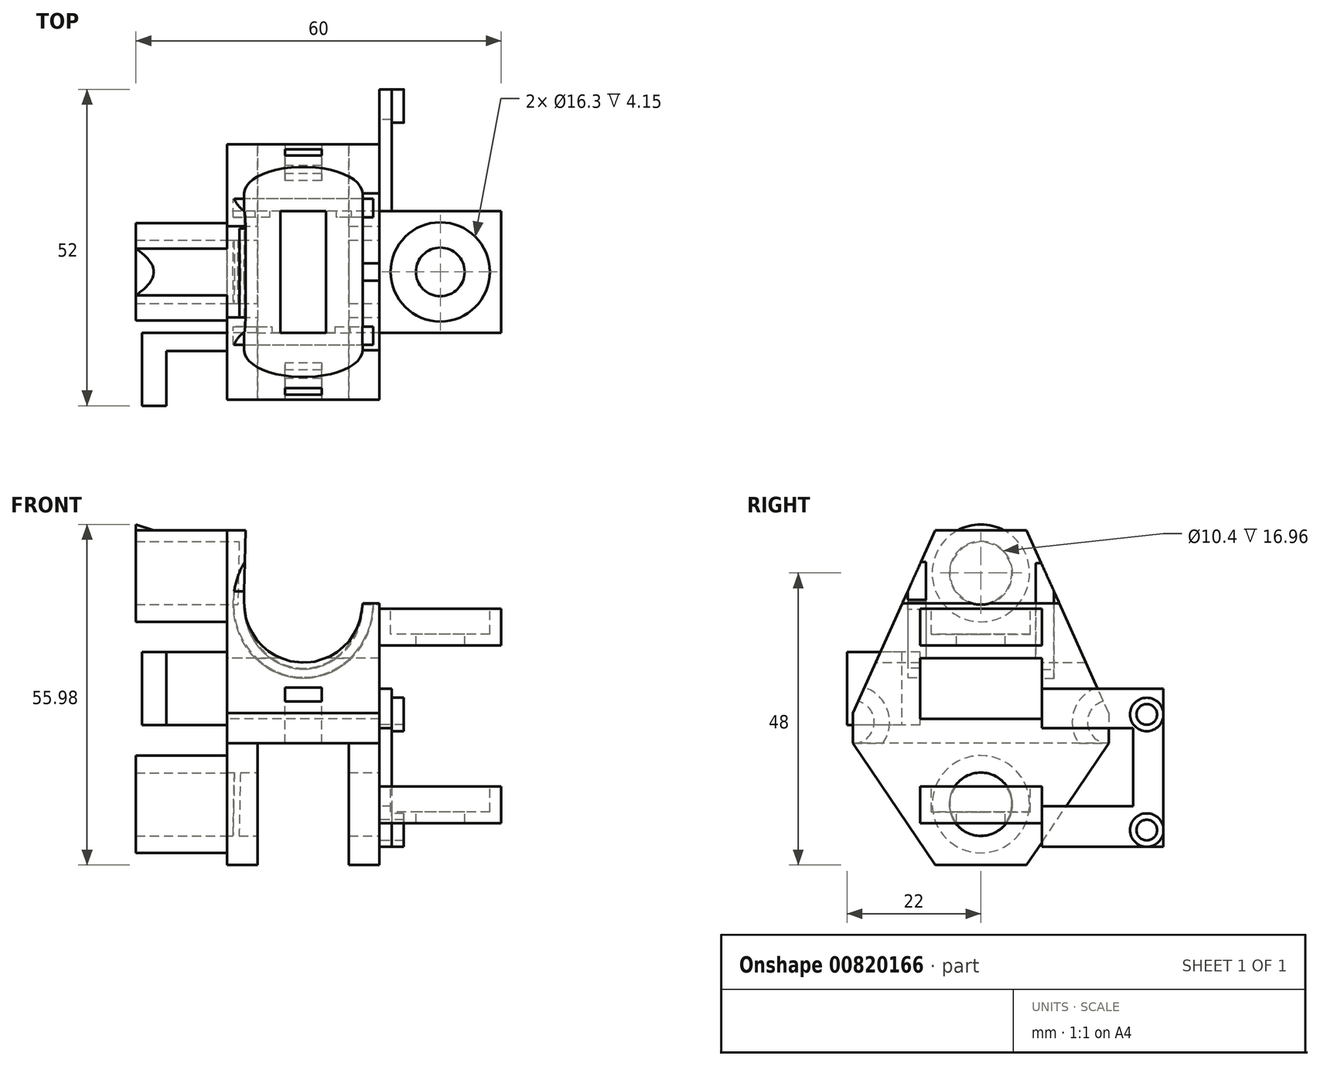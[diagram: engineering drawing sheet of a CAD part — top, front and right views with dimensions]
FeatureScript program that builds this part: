
annotation { "Feature Type Name" : "Feature", "Feature Type Description" : "" }
export const myFeature = defineFeature(function(context is Context, id is Id, definition is map)
    precondition{}
    {
        {
            var Q0;
            Q0=qCreatedBy(makeId("Top.planeOp"),FACE);
            var sketch = newSketch(context, id + "F0", { "sketchPlane" : qUnion([Q0])});
            skLineSegment(sketch, "E0.bottom", {"start": v(0, 0) * mm, "end": v(42, 0) * mm});
            skLineSegment(sketch, "E0.top", {"start": v(0, 42) * mm, "end": v(42, 42) * mm});
            skLineSegment(sketch, "E0.left", {"start": v(0, 0) * mm, "end": v(0, 42) * mm});
            skLineSegment(sketch, "E0.right", {"start": v(42, 0) * mm, "end": v(42, 12) * mm});
            skArc(sketch, "E1", {"start": v(27.05, 31.36) * mm, "mid": v(9, 21) * mm, "end": v(27.05, 10.64) * mm});
            skPoint(sketch, "E1.centerSnap0", {"position": v(21, 42) * mm});
            skPoint(sketch, "E1.centerSnap1", {"position": v(42, 21) * mm});
            skCircle(sketch, "E2", {"center": v(5.5, 36.5) * mm, "radius": 1.55 * mm});
            skCircle(sketch, "E3", {"center": v(36.5, 36.5) * mm, "radius": 1.55 * mm});
            skCircle(sketch, "E4", {"center": v(36.5, 5.5) * mm, "radius": 1.55 * mm});
            skCircle(sketch, "E5", {"center": v(5.5, 5.5) * mm, "radius": 1.55 * mm});
            skLineSegment(sketch, "E6", {"start": v(42, 30) * mm, "end": v(32.1, 30) * mm});
            skLineSegment(sketch, "E7", {"start": v(42, 12) * mm, "end": v(32.1, 12) * mm});
            skLineSegment(sketch, "E8.trimOffspring", {"start": v(42, 30) * mm, "end": v(42, 42) * mm});
            skPoint(sketch, "E9.visualSharp", {"position": v(28.94, 30) * mm});
            skArc(sketch, "E9.filletArc", {"start": v(27.05, 31.36) * mm, "mid": v(29.48, 30.35) * mm, "end": v(32.1, 30) * mm});
            skPoint(sketch, "E10.visualSharp", {"position": v(28.94, 12) * mm});
            skArc(sketch, "E10.filletArc", {"start": v(32.1, 12) * mm, "mid": v(29.48, 11.65) * mm, "end": v(27.05, 10.64) * mm});
            skSolve(sketch);
        }
        {
            var Q0;
            Q0=qSketchRegion(id+"F0",true);
            extrude(context, id + "F1", {"entities" : qUnion([Q0]), "depth" : 5 * mm, "offsetDistance" : 25 * mm});
        }
        {
            var Q0;
            Q0=makeQuery(id+"F1.opExtrude","SWEPT_FACE",FACE,{"disambiguationData":[OSD([sQuery(id+"F0.wireOp",EDGE,"E0.left")])]});
            var sketch = newSketch(context, id + "F2", { "sketchPlane" : qUnion([Q0])});
            skLineSegment(sketch, "E11", {"start": v(-42, 5) * mm, "end": v(-28.5, 35) * mm});
            skLineSegment(sketch, "E12", {"start": v(-28.5, 35) * mm, "end": v(-13.5, 35) * mm});
            skLineSegment(sketch, "E13", {"start": v(-13.5, 35) * mm, "end": v(0, 5) * mm});
            skLineSegment(sketch, "E14", {"start": v(0, 5) * mm, "end": v(0, 0) * mm});
            skLineSegment(sketch, "E15", {"start": v(0, 0) * mm, "end": v(-13.5, -20) * mm});
            skLineSegment(sketch, "E16", {"start": v(-13.5, -20) * mm, "end": v(-28.5, -20) * mm});
            skLineSegment(sketch, "E17", {"start": v(-28.5, -20) * mm, "end": v(-42, 0) * mm});
            skLineSegment(sketch, "E18", {"start": v(-42, 0) * mm, "end": v(-42, 5) * mm});
            skLineSegment(sketch, "E19.bottom", {"start": v(-31, 5) * mm, "end": v(-11, 5) * mm});
            skLineSegment(sketch, "E19.top", {"start": v(-31, 13) * mm, "end": v(-11, 13) * mm});
            skLineSegment(sketch, "E19.left", {"start": v(-31, 5) * mm, "end": v(-31, 13) * mm});
            skLineSegment(sketch, "E19.right", {"start": v(-11, 5) * mm, "end": v(-11, 13) * mm});
            skCircle(sketch, "E20", {"center": v(-21, 28) * mm, "radius": 5.2 * mm});
            skPoint(sketch, "E20.centerSnap0", {"position": v(-21, 13) * mm});
            skCircle(sketch, "E21", {"center": v(-21, -10) * mm, "radius": 5.2 * mm});
            skPoint(sketch, "E21.centerSnap0", {"position": v(-21, 0) * mm});
            skSolve(sketch);
        }
        {
            var Q0;
            Q0=qSketchRegion(id+"F2",true);
            extrude(context, id + "F3", {"entities" : qUnion([Q0]), "operationType" : NewBodyOperationType.ADD, "depth" : 25 * mm, "offsetDistance" : 25 * mm});
        }
        {
            var Q0;
            Q0=makeQuery(id+"F3.boolean.opBoolean","MERGE",FACE,{"derivedFrom":[makeQuery(id+"F1.opExtrude","SWEPT_FACE",FACE,{"disambiguationData":[OSD([sQuery(id+"F0.wireOp",EDGE,"E0.bottom")])]}),makeQuery(id+"F3.opExtrude","SWEPT_FACE",FACE,{"disambiguationData":[OSD([sQuery(id+"F2.wireOp",EDGE,"E14")])]})]});
            var sketch = newSketch(context, id + "F4", { "sketchPlane" : qUnion([Q0])});
            skArc(sketch, "E22", {"start": v(-22.25, 23.2) * mm, "mid": v(-12.6, 13.25) * mm, "end": v(-2.75, 23) * mm});
            skLineSegment(sketch, "E23.bottom", {"start": v(-20, 0) * mm, "end": v(-5, 0) * mm});
            skLineSegment(sketch, "E23.top", {"start": v(-20, -20) * mm, "end": v(-5, -20) * mm});
            skLineSegment(sketch, "E23.left", {"start": v(-20, 0) * mm, "end": v(-20, -20) * mm});
            skLineSegment(sketch, "E23.right", {"start": v(-5, 0) * mm, "end": v(-5, -20) * mm});
            skLineSegment(sketch, "E24", {"start": v(-2.75, 23) * mm, "end": v(0, 23) * mm});
            skLineSegment(sketch, "E25", {"start": v(0, 23) * mm, "end": v(0, 35.11) * mm});
            skLineSegment(sketch, "E26", {"start": v(0, 35.11) * mm, "end": v(-22, 35.11) * mm});
            skLineSegment(sketch, "E27", {"start": v(-22, 35.11) * mm, "end": v(-22.25, 23) * mm});
            skSolve(sketch);
        }
        {
            var Q0;
            Q0=qSketchRegion(id+"F4",true);
            extrude(context, id + "F5", {"entities" : qUnion([Q0]), "operationType" : NewBodyOperationType.REMOVE, "oppositeDirection" : true, "depth" : 69 * mm, "offsetDistance" : 25 * mm});
        }
        {
            var Q0;
            Q0=makeQuery(id+"F3.opExtrude","CAP_FACE",FACE,{"disambiguationData":[OSD([sQuery(id+"F2.wireOp",EDGE,"E11"),sQuery(id+"F2.wireOp",EDGE,"E12"),sQuery(id+"F2.wireOp",EDGE,"E13"),sQuery(id+"F2.wireOp",EDGE,"E14"),sQuery(id+"F2.wireOp",EDGE,"E15"),sQuery(id+"F2.wireOp",EDGE,"E16"),sQuery(id+"F2.wireOp",EDGE,"E17"),sQuery(id+"F2.wireOp",EDGE,"E18"),sQuery(id+"F2.wireOp",EDGE,"E19.bottom"),sQuery(id+"F2.wireOp",EDGE,"E19.top"),sQuery(id+"F2.wireOp",EDGE,"E19.left"),sQuery(id+"F2.wireOp",EDGE,"E19.right"),sQuery(id+"F2.wireOp",EDGE,"E20"),sQuery(id+"F2.wireOp",EDGE,"E21")])],"isStart":false});
            var sketch = newSketch(context, id + "F6", { "sketchPlane" : qUnion([Q0])});
            skArc(sketch, "E28", {"start": v(-26.2, 28) * mm, "mid": v(-21, 22.8) * mm, "end": v(-15.8, 28) * mm});
            skArc(sketch, "E29", {"start": v(-29, 28) * mm, "mid": v(-21, 19.98) * mm, "end": v(-13, 28) * mm});
            skArc(sketch, "E30", {"start": v(-29, -10) * mm, "mid": v(-21, -18) * mm, "end": v(-13, -10) * mm});
            skArc(sketch, "E31", {"start": v(-26.2, -10) * mm, "mid": v(-21, -15.24) * mm, "end": v(-15.8, -10) * mm});
            skArc(sketch, "E32", {"start": v(-13, 28) * mm, "mid": v(-21, 35.98) * mm, "end": v(-29, 28) * mm});
            skArc(sketch, "E33", {"start": v(-15.8, 28) * mm, "mid": v(-21, 33.2) * mm, "end": v(-26.2, 28) * mm});
            skArc(sketch, "E34", {"start": v(-13, -10) * mm, "mid": v(-21, -2) * mm, "end": v(-29, -10) * mm});
            skArc(sketch, "E35", {"start": v(-15.8, -10) * mm, "mid": v(-21, -4.84) * mm, "end": v(-26.2, -10) * mm});
            skSolve(sketch);
        }
        {
            var Q0;
            Q0=qSketchRegion(id+"F6",true);
            extrude(context, id + "F7", {"entities" : qUnion([Q0]), "operationType" : NewBodyOperationType.ADD, "depth" : 15 * mm, "offsetDistance" : 25 * mm});
        }
        {
            var Q0;
            Q0=makeQuery(id+"F3.boolean.opBoolean","MERGE",FACE,{"derivedFrom":[makeQuery(id+"F1.opExtrude","SWEPT_FACE",FACE,{"disambiguationData":[OSD([sQuery(id+"F0.wireOp",EDGE,"E0.bottom")])]}),makeQuery(id+"F3.opExtrude","SWEPT_FACE",FACE,{"disambiguationData":[OSD([sQuery(id+"F2.wireOp",EDGE,"E14")])]})]});
            cPlane(context, id + "F8", {"entities" : qUnion([Q0]), "cplaneType" : CPlaneType.OFFSET, "offset" : 9 * mm, "oppositeDirection" : true, "width" : 150 * mm, "height" : 150 * mm});
        }
        {
            var Q0;
            Q0=qCreatedBy(id+"F8.planeOp",FACE);
            var sketch = newSketch(context, id + "F9", { "sketchPlane" : qUnion([Q0])});
            skEllipse(sketch, "E36", {"center": v(-12.5, 23.1) * mm, "majorRadius": 10.75 * mm, "minorRadius": 9.75 * mm, "majorAxis": v(0, -1)});
            skEllipse(sketch, "E37", {"center": v(-12.5, 23.1) * mm, "majorRadius": 12.25 * mm, "minorRadius": 11.5 * mm, "majorAxis": v(0, -1)});
            skSolve(sketch);
        }
        {
            var Q0;
            Q0=qSketchRegion(id+"F9",true);
            extrude(context, id + "F10", {"entities" : qUnion([Q0]), "operationType" : NewBodyOperationType.REMOVE, "oppositeDirection" : true, "depth" : 3 * mm, "offsetDistance" : 25 * mm});
        }
        {
            var Q0;
            Q0=makeQuery(id+"F3.boolean.opBoolean","MERGE",FACE,{"derivedFrom":[makeQuery(id+"F1.opExtrude","SWEPT_FACE",FACE,{"disambiguationData":[OSD([sQuery(id+"F0.wireOp",EDGE,"E0.top")])]}),makeQuery(id+"F3.opExtrude","SWEPT_FACE",FACE,{"disambiguationData":[OSD([sQuery(id+"F2.wireOp",EDGE,"E18")])]})]});
            cPlane(context, id + "F11", {"entities" : qUnion([Q0]), "cplaneType" : CPlaneType.OFFSET, "offset" : 9 * mm, "oppositeDirection" : true, "width" : 150 * mm, "height" : 150 * mm});
        }
        {
            var Q0;
            Q0=qCreatedBy(id+"F11.planeOp",FACE);
            var sketch = newSketch(context, id + "F12", { "sketchPlane" : qUnion([Q0])});
            skEllipse(sketch, "E38", {"center": v(12.5, 22.9) * mm, "majorRadius": 10.75 * mm, "minorRadius": 9.75 * mm, "majorAxis": v(0, -1)});
            skEllipse(sketch, "E39", {"center": v(12.5, 22.9) * mm, "majorRadius": 12.25 * mm, "minorRadius": 11.5 * mm, "majorAxis": v(0, -1)});
            skSolve(sketch);
        }
        {
            var Q0;
            Q0=qSketchRegion(id+"F12",true);
            extrude(context, id + "F13", {"entities" : qUnion([Q0]), "operationType" : NewBodyOperationType.REMOVE, "oppositeDirection" : true, "depth" : 3 * mm, "offsetDistance" : 25 * mm});
        }
        {
            var Q0;
            {var subQ0=sQuery(id+"F0.wireOp",EDGE,"E0.bottom");var subQ1=sQuery(id+"F2.wireOp",EDGE,"E21");var subQ2=sQuery(id+"F2.wireOp",EDGE,"E20");var subQ3=sQuery(id+"F2.wireOp",EDGE,"E19.top");var subQ4=sQuery(id+"F2.wireOp",EDGE,"E18");var subQ5=sQuery(id+"F2.wireOp",EDGE,"E17");var subQ6=sQuery(id+"F2.wireOp",EDGE,"E11");var subQ7=sQuery(id+"F6.wireOp",EDGE,"j4Je13ar-cUgQ-P9dA-qSxm-OQoqqm40TVXU");var subQ8=sQuery(id+"F2.wireOp",EDGE,"E19.right");var subQ9=sQuery(id+"F0.wireOp",EDGE,"E0.top");var subQ10=sQuery(id+"F6.wireOp",EDGE,"E31");var subQ11=sQuery(id+"F6.wireOp",EDGE,"E30");var subQ12=sQuery(id+"F6.wireOp",EDGE,"HeXZzPOW-6o9y-4eNm-dmXj-kad8RJGDjiKm");var subQ13=sQuery(id+"F2.wireOp",EDGE,"E19.left");var subQ14=sQuery(id+"F2.wireOp",EDGE,"E19.bottom");var subQ15=sQuery(id+"F2.wireOp",EDGE,"E15");var subQ16=sQuery(id+"F2.wireOp",EDGE,"E16");var subQ17=sQuery(id+"F2.wireOp",EDGE,"E14");var subQ18=sQuery(id+"F2.wireOp",EDGE,"E13");var subQ19=sQuery(id+"F2.wireOp",EDGE,"E12");var subQ20=makeQuery(id+"F3.opExtrude","CAP_FACE",FACE,{"disambiguationData":[OSD([subQ6,subQ19,subQ18,subQ17,subQ15,subQ16,subQ5,subQ4,subQ14,subQ3,subQ13,subQ8,subQ2,subQ1])],"isStart":false});Q0=makeQuery(id+"F7.boolean.opBoolean","SPLIT",FACE,{"disambiguationData":[TD([makeQuery(id+"F1.opExtrude","SWEPT_FACE",FACE,{"disambiguationData":[OSD([subQ0])]}),makeQuery(id+"F1.opExtrude","CAP_FACE",FACE,{"disambiguationData":[OSD([subQ0,subQ9,sQuery(id+"F0.wireOp",EDGE,"E0.left"),sQuery(id+"F0.wireOp",EDGE,"E0.right"),sQuery(id+"F0.wireOp",EDGE,"E1"),sQuery(id+"F0.wireOp",EDGE,"E2"),sQuery(id+"F0.wireOp",EDGE,"E3"),sQuery(id+"F0.wireOp",EDGE,"E4"),sQuery(id+"F0.wireOp",EDGE,"E5"),sQuery(id+"F0.wireOp",EDGE,"E6"),sQuery(id+"F0.wireOp",EDGE,"E7"),sQuery(id+"F0.wireOp",EDGE,"E8.trimOffspring"),sQuery(id+"F0.wireOp",EDGE,"E9.filletArc"),sQuery(id+"F0.wireOp",EDGE,"E10.filletArc")])],"isStart":false}),makeQuery(id+"F1.opExtrude","SWEPT_FACE",FACE,{"disambiguationData":[OSD([subQ9])]}),makeQuery(id+"F3.opExtrude","SWEPT_FACE",FACE,{"disambiguationData":[OSD([subQ6])]}),subQ20,makeQuery(id+"F3.opExtrude","SWEPT_FACE",FACE,{"disambiguationData":[OSD([subQ19])]}),makeQuery(id+"F3.opExtrude","SWEPT_FACE",FACE,{"disambiguationData":[OSD([subQ18])]}),makeQuery(id+"F3.opExtrude","SWEPT_FACE",FACE,{"disambiguationData":[OSD([subQ17])]}),makeQuery(id+"F3.opExtrude","SWEPT_FACE",FACE,{"disambiguationData":[OSD([subQ15])]}),makeQuery(id+"F3.opExtrude","SWEPT_FACE",FACE,{"disambiguationData":[OSD([subQ16])]}),makeQuery(id+"F3.opExtrude","SWEPT_FACE",FACE,{"disambiguationData":[OSD([subQ5])]}),makeQuery(id+"F3.opExtrude","SWEPT_FACE",FACE,{"disambiguationData":[OSD([subQ4])]}),makeQuery(id+"F3.opExtrude","SWEPT_FACE",FACE,{"disambiguationData":[OSD([subQ14])]}),makeQuery(id+"F3.opExtrude","SWEPT_FACE",FACE,{"disambiguationData":[OSD([subQ3])]}),makeQuery(id+"F3.opExtrude","SWEPT_FACE",FACE,{"disambiguationData":[OSD([subQ13])]}),makeQuery(id+"F3.opExtrude","SWEPT_FACE",FACE,{"disambiguationData":[OSD([subQ8])]}),makeQuery(id+"F3.opExtrude","SWEPT_FACE",FACE,{"disambiguationData":[OSD([subQ2])]}),makeQuery(id+"F3.opExtrude","SWEPT_FACE",FACE,{"disambiguationData":[OSD([subQ1])]}),makeQuery(id+"F7.opExtrude","SWEPT_FACE",FACE,{"disambiguationData":[OSD([sQuery(id+"F6.wireOp",EDGE,"1yMtYrWf-nUJP-NBpX-7LZj-JU54sDcnYQW7")])]}),makeQuery(id+"F7.opExtrude","SWEPT_FACE",FACE,{"disambiguationData":[OSD([sQuery(id+"F6.wireOp",EDGE,"Y7kda9e2-xFBF-SAdd-E8dt-nTogyCoIO5LO")])]}),makeQuery(id+"F7.opExtrude","SWEPT_FACE",FACE,{"disambiguationData":[OSD([sQuery(id+"F6.wireOp",EDGE,"E28")])]}),makeQuery(id+"F7.opExtrude","SWEPT_FACE",FACE,{"disambiguationData":[OSD([sQuery(id+"F6.wireOp",EDGE,"E29")])]}),makeQuery(id+"F7.opExtrude","SWEPT_FACE",FACE,{"disambiguationData":[OSD([subQ12])]}),makeQuery(id+"F7.opExtrude","CAP_FACE",FACE,{"disambiguationData":[OSD([subQ12,subQ11,subQ7,subQ10])],"isStart":true}),makeQuery(id+"F7.opExtrude","SWEPT_FACE",FACE,{"disambiguationData":[OSD([subQ11])]}),makeQuery(id+"F7.opExtrude","SWEPT_FACE",FACE,{"disambiguationData":[OSD([subQ7])]}),makeQuery(id+"F7.opExtrude","SWEPT_FACE",FACE,{"disambiguationData":[OSD([subQ10])]})])],"derivedFrom":subQ20});}
            cPlane(context, id + "F14", {"entities" : qUnion([Q0]), "cplaneType" : CPlaneType.OFFSET, "offset" : 9.5 * mm, "oppositeDirection" : true, "width" : 150 * mm, "height" : 150 * mm});
        }
        {
            var Q0;
            Q0=qCreatedBy(id+"F14.planeOp",FACE);
            var sketch = newSketch(context, id + "F15", { "sketchPlane" : qUnion([Q0])});
            skCircle(sketch, "E40", {"center": v(0, 3.5) * mm, "radius": 3.5 * mm});
            skCircle(sketch, "E41", {"center": v(0, 3.5) * mm, "radius": 6 * mm});
            skCircle(sketch, "E42", {"center": v(-42, 3.5) * mm, "radius": 3.5 * mm});
            skCircle(sketch, "E43", {"center": v(-42, 3.5) * mm, "radius": 6 * mm});
            skSolve(sketch);
        }
        {
            var Q0;
            Q0=qSketchRegion(id+"F15",true);
            extrude(context, id + "F16", {"entities" : qUnion([Q0]), "operationType" : NewBodyOperationType.REMOVE, "oppositeDirection" : true, "depth" : 6 * mm, "offsetDistance" : 25 * mm});
        }
        {
            var Q0;
            {var subQ0=sQuery(id+"F2.wireOp",EDGE,"E16");var subQ1=sQuery(id+"F2.wireOp",EDGE,"E14");var subQ2=sQuery(id+"F2.wireOp",EDGE,"E13");var subQ3=sQuery(id+"F2.wireOp",EDGE,"E12");var subQ4=sQuery(id+"F2.wireOp",EDGE,"E15");var subQ5=sQuery(id+"F0.wireOp",EDGE,"E0.bottom");var subQ6=sQuery(id+"F2.wireOp",EDGE,"E19.bottom");var subQ7=sQuery(id+"F2.wireOp",EDGE,"E17");var subQ9=sQuery(id+"F2.wireOp",EDGE,"E19.left");var subQ12=sQuery(id+"F2.wireOp",EDGE,"E19.right");var subQ13=sQuery(id+"F2.wireOp",EDGE,"E11");var subQ14=sQuery(id+"F2.wireOp",EDGE,"E18");var subQ15=sQuery(id+"F2.wireOp",EDGE,"E19.top");Q0=makeQuery(id+"F7.boolean.opBoolean","SPLIT",FACE,{"disambiguationData":[TD([makeQuery(id+"F1.opExtrude","SWEPT_FACE",FACE,{"disambiguationData":[OSD([subQ5])]})])],"derivedFrom":makeQuery(id+"F3.opExtrude","CAP_FACE",FACE,{"disambiguationData":[OSD([subQ13,subQ3,subQ2,subQ1,subQ4,subQ0,subQ7,subQ14,subQ6,subQ15,subQ9,subQ12,sQuery(id+"F2.wireOp",EDGE,"E20"),sQuery(id+"F2.wireOp",EDGE,"E21")])],"isStart":false})});}
            var sketch = newSketch(context, id + "F17", { "sketchPlane" : qUnion([Q0])});
            skLineSegment(sketch, "E44.bottom", {"start": v(-31, 4) * mm, "end": v(-11, 4) * mm});
            skLineSegment(sketch, "E44.top", {"start": v(-31, 14) * mm, "end": v(-11, 14) * mm});
            skLineSegment(sketch, "E44.left", {"start": v(-31, 4) * mm, "end": v(-31, 14) * mm});
            skLineSegment(sketch, "E44.right", {"start": v(-11, 4) * mm, "end": v(-11, 14) * mm});
            skSolve(sketch);
        }
        {
            var Q0;
            Q0=qSketchRegion(id+"F17",true);
            extrude(context, id + "F18", {"entities" : qUnion([Q0]), "operationType" : NewBodyOperationType.REMOVE, "oppositeDirection" : true, "depth" : 50 * mm, "offsetDistance" : 25 * mm});
        }
        {
            var Q0;
            {var subQ0=sQuery(id+"F6.wireOp",EDGE,"E32");var subQ1=sQuery(id+"F6.wireOp",EDGE,"E29");Q0=makeQuery(id+"F7.boolean.opBoolean","SPLIT",EDGE,{"disambiguationData":[topologyDisambiguationEdgeConnected([makeQuery(id+"F3.opExtrude","CAP_FACE",FACE,{"disambiguationData":[OSD([sQuery(id+"F2.wireOp",EDGE,"E11"),sQuery(id+"F2.wireOp",EDGE,"E12"),sQuery(id+"F2.wireOp",EDGE,"E13"),sQuery(id+"F2.wireOp",EDGE,"E14"),sQuery(id+"F2.wireOp",EDGE,"E15"),sQuery(id+"F2.wireOp",EDGE,"E16"),sQuery(id+"F2.wireOp",EDGE,"E17"),sQuery(id+"F2.wireOp",EDGE,"E18"),sQuery(id+"F2.wireOp",EDGE,"E19.bottom"),sQuery(id+"F2.wireOp",EDGE,"E19.top"),sQuery(id+"F2.wireOp",EDGE,"E19.left"),sQuery(id+"F2.wireOp",EDGE,"E19.right"),sQuery(id+"F2.wireOp",EDGE,"E20"),sQuery(id+"F2.wireOp",EDGE,"E21")])],"isStart":false})])],"derivedFrom":makeQuery(id+"F7.opExtrude","CAP_EDGE",EDGE,{"disambiguationData":[OSD([subQ1,subQ0])],"isStart":true})});}
            var Q1;
            Q1=makeQuery(id+"F7.opExtrude","CAP_EDGE",EDGE,{"disambiguationData":[OSD([sQuery(id+"F6.wireOp",EDGE,"E30"),sQuery(id+"F6.wireOp",EDGE,"E34")])],"isStart":true});
            chamfer(context, id + "F19", {"entities" : qUnion([Q0, Q1]), "chamferType" : ChamferType.TWO_OFFSETS, "width1" : 15 * mm, "oppositeDirection" : false, "width2" : 5 * mm, "tangentPropagation" : true});
        }
        {
            var Q0;
            {var subQ4=makeQuery(id+"F5.boolean.opBoolean","COPY",FACE,{"derivedFrom":makeQuery(id+"F5.opExtrude","SWEPT_FACE",FACE,{"disambiguationData":[OSD([sQuery(id+"F4.wireOp",EDGE,"E27")])]})});Q0=makeQuery(id+"F13.boolean.opBoolean","SPLIT",FACE,{"disambiguationData":[TD([makeQuery(id+"F3.opExtrude","SWEPT_FACE",FACE,{"disambiguationData":[OSD([sQuery(id+"F2.wireOp",EDGE,"E12")])]})])],"derivedFrom":subQ4});}
            var sketch = newSketch(context, id + "F20", { "sketchPlane" : qUnion([Q0])});
            skLineSegment(sketch, "E45.bottom", {"start": v(13.6, 0) * mm, "end": v(29.55, 0) * mm});
            skLineSegment(sketch, "E45.top", {"start": v(13.6, -17.05) * mm, "end": v(29.55, -17.05) * mm});
            skLineSegment(sketch, "E45.left", {"start": v(13.6, 0) * mm, "end": v(13.6, -17.05) * mm});
            skLineSegment(sketch, "E45.right", {"start": v(29.55, 0) * mm, "end": v(29.55, -17.05) * mm});
            skLineSegment(sketch, "E46.bottom", {"start": v(13.5, 34.53) * mm, "end": v(28.12, 34.53) * mm});
            skLineSegment(sketch, "E46.top", {"start": v(13.5, 19.84) * mm, "end": v(28.12, 19.84) * mm});
            skLineSegment(sketch, "E46.left", {"start": v(13.5, 34.53) * mm, "end": v(13.5, 19.84) * mm});
            skLineSegment(sketch, "E46.right", {"start": v(28.12, 34.53) * mm, "end": v(28.12, 19.84) * mm});
            skSolve(sketch);
        }
        {
            var Q0;
            Q0=qSketchRegion(id+"F20",true);
            extrude(context, id + "F21", {"entities" : qUnion([Q0]), "operationType" : NewBodyOperationType.ADD, "oppositeDirection" : true, "depth" : 1 * mm, "offsetDistance" : 25 * mm});
        }
        {
            var Q0;
            {var subQ0=sQuery(id+"F2.wireOp",EDGE,"E19.bottom");var subQ2=sQuery(id+"F2.wireOp",EDGE,"E14");var subQ3=sQuery(id+"F2.wireOp",EDGE,"E13");var subQ4=sQuery(id+"F2.wireOp",EDGE,"E12");var subQ6=sQuery(id+"F2.wireOp",EDGE,"E19.left");var subQ7=sQuery(id+"F2.wireOp",EDGE,"E18");var subQ8=sQuery(id+"F2.wireOp",EDGE,"E19.right");var subQ9=sQuery(id+"F2.wireOp",EDGE,"E19.top");var subQ10=sQuery(id+"F2.wireOp",EDGE,"E11");var subQ11=sQuery(id+"F2.wireOp",EDGE,"E20");Q0=makeQuery(id+"F3.boolean.opBoolean","SPLIT",FACE,{"disambiguationData":[TD([makeQuery(id+"F3.opExtrude","SWEPT_FACE",FACE,{"disambiguationData":[OSD([subQ10])]})])],"derivedFrom":makeQuery(id+"F3.opExtrude","CAP_FACE",FACE,{"disambiguationData":[OSD([subQ10,subQ4,subQ3,subQ2,sQuery(id+"F2.wireOp",EDGE,"E15"),sQuery(id+"F2.wireOp",EDGE,"E16"),sQuery(id+"F2.wireOp",EDGE,"E17"),subQ7,subQ0,subQ9,subQ6,subQ8,subQ11,sQuery(id+"F2.wireOp",EDGE,"E21")])],"isStart":true})});}
            var sketch = newSketch(context, id + "F22", { "sketchPlane" : qUnion([Q0])});
            skLineSegment(sketch, "E47.bottom", {"start": v(-2.56, 16.52) * mm, "end": v(48.7, 16.52) * mm});
            skLineSegment(sketch, "E47.top", {"start": v(-2.56, -9.4) * mm, "end": v(48.7, -9.4) * mm});
            skLineSegment(sketch, "E47.left", {"start": v(-2.56, 16.52) * mm, "end": v(-2.56, -9.4) * mm});
            skLineSegment(sketch, "E47.right", {"start": v(48.7, 16.52) * mm, "end": v(48.7, -9.4) * mm});
            skSolve(sketch);
        }
        {
            var Q0;
            Q0 = qSketchRegion(id + "F22", true);
            extrude(context, id + "F23", {"entities" : qUnion([Q0]), "operationType" : NewBodyOperationType.REMOVE, "depth" : 50 * mm, "offsetDistance" : 25 * mm});
        }
        {
            var Q0;
            {var subQ0=sQuery(id+"F2.wireOp",EDGE,"E19.bottom");var subQ3=sQuery(id+"F2.wireOp",EDGE,"E14");var subQ5=sQuery(id+"F2.wireOp",EDGE,"E13");var subQ6=sQuery(id+"F2.wireOp",EDGE,"E12");var subQ20=sQuery(id+"F2.wireOp",EDGE,"E19.left");var subQ21=sQuery(id+"F2.wireOp",EDGE,"E18");var subQ24=sQuery(id+"F2.wireOp",EDGE,"E19.right");var subQ25=sQuery(id+"F2.wireOp",EDGE,"E19.top");var subQ26=sQuery(id+"F2.wireOp",EDGE,"E11");var subQ27=sQuery(id+"F2.wireOp",EDGE,"E20");var subQ28=sQuery(id+"F2.wireOp",EDGE,"E21");var subQ29=sQuery(id+"F2.wireOp",EDGE,"E17");var subQ30=sQuery(id+"F2.wireOp",EDGE,"E16");var subQ31=sQuery(id+"F2.wireOp",EDGE,"E15");var subQ32=makeQuery(id+"F3.opExtrude","CAP_FACE",FACE,{"disambiguationData":[OSD([subQ26,subQ6,subQ5,subQ3,subQ31,subQ30,subQ29,subQ21,subQ0,subQ25,subQ20,subQ24,subQ27,subQ28])],"isStart":true});Q0=makeQuery(id+"F23.boolean.opBoolean","MERGE",FACE,{"derivedFrom":[makeQuery(id+"F3.boolean.opBoolean","SPLIT",FACE,{"disambiguationData":[TD([makeQuery(id+"F3.opExtrude","SWEPT_FACE",FACE,{"disambiguationData":[OSD([subQ31])]})])],"derivedFrom":subQ32}),makeQuery(id+"F3.boolean.opBoolean","SPLIT",FACE,{"disambiguationData":[TD([makeQuery(id+"F3.opExtrude","SWEPT_FACE",FACE,{"disambiguationData":[OSD([subQ26])]})])],"derivedFrom":subQ32}),makeQuery(id+"F23.opExtrude","CAP_FACE",FACE,{"disambiguationData":[OSD([sQuery(id+"F22.wireOp",EDGE,"E47.bottom"),sQuery(id+"F22.wireOp",EDGE,"E47.top"),sQuery(id+"F22.wireOp",EDGE,"E47.left"),sQuery(id+"F22.wireOp",EDGE,"E47.right")])],"isStart":true})]});}
            var sketch = newSketch(context, id + "F24", { "sketchPlane" : qUnion([Q0])});
            skLineSegment(sketch, "E48.bottom", {"start": v(11, 16.11) * mm, "end": v(31, 16.11) * mm});
            skLineSegment(sketch, "E48.top", {"start": v(11, 22.11) * mm, "end": v(31, 22.11) * mm});
            skLineSegment(sketch, "E48.left", {"start": v(11, 16.11) * mm, "end": v(11, 22.11) * mm});
            skLineSegment(sketch, "E48.right", {"start": v(31, 16.11) * mm, "end": v(31, 22.11) * mm});
            skLineSegment(sketch, "E49.bottom", {"start": v(11, -7.1) * mm, "end": v(31, -7.1) * mm});
            skLineSegment(sketch, "E49.top", {"start": v(11, -13.1) * mm, "end": v(31, -13.1) * mm});
            skLineSegment(sketch, "E49.left", {"start": v(11, -7.1) * mm, "end": v(11, -13.1) * mm});
            skLineSegment(sketch, "E49.right", {"start": v(31, -7.1) * mm, "end": v(31, -13.1) * mm});
            skSolve(sketch);
        }
        {
            var Q0;
            Q0 = qSketchRegion(id + "F24", true);
            extrude(context, id + "F25", {"entities" : qUnion([Q0]), "operationType" : NewBodyOperationType.ADD, "depth" : 20 * mm, "offsetDistance" : 25 * mm});
        }
        {
            var Q0;
            Q0=makeQuery(id+"F25.opExtrude","SWEPT_FACE",FACE,{"disambiguationData":[OSD([sQuery(id+"F24.wireOp",EDGE,"E48.top")])]});
            var sketch = newSketch(context, id + "F26", { "sketchPlane" : qUnion([Q0])});
            skPoint(sketch, "E50.centerSnap0", {"position": v(10, 31) * mm});
            skPoint(sketch, "E50.centerSnap1", {"position": v(20, 21) * mm});
            skCircle(sketch, "E51", {"center": v(10, 21) * mm, "radius": 4 * mm});
            skSolve(sketch);
        }
        {
            var Q0;
            Q0=makeQuery(id+"F26.imprint","IMPRINT",FACE,{"disambiguationData":[TD([[makeQuery(id+"F26.imprint","IMPRINT",EDGE,{"derivedFrom":sQuery(id+"F26.wireOp",EDGE,"E51")}),1.0]])]});
            extrude(context, id + "F27", {"entities" : qUnion([Q0]), "operationType" : NewBodyOperationType.REMOVE, "endBound" : BoundingType.THROUGH_ALL, "oppositeDirection" : true, "depth" : 25 * mm, "offsetDistance" : 25 * mm});
        }
        {
            var Q0;
            Q0=makeQuery(id+"F25.opExtrude","SWEPT_FACE",FACE,{"disambiguationData":[OSD([sQuery(id+"F24.wireOp",EDGE,"E48.top")])]});
            var sketch = newSketch(context, id + "F28", { "sketchPlane" : qUnion([Q0])});
            skCircle(sketch, "E52", {"center": v(10, 21) * mm, "radius": 8.15 * mm});
            skSolve(sketch);
        }
        {
            var Q0;
            Q0 = qSketchRegion(id + "F28", true);
            extrude(context, id + "F29", {"entities" : qUnion([Q0]), "operationType" : NewBodyOperationType.REMOVE, "oppositeDirection" : true, "depth" : 4.15 * mm, "offsetDistance" : 25 * mm});
        }
        {
            var Q0;
            Q0=makeQuery(id+"F25.opExtrude","SWEPT_FACE",FACE,{"disambiguationData":[OSD([sQuery(id+"F24.wireOp",EDGE,"E49.bottom")])]});
            var sketch = newSketch(context, id + "F30", { "sketchPlane" : qUnion([Q0])});
            skCircle(sketch, "E53", {"center": v(10, 21) * mm, "radius": 8.15 * mm});
            skSolve(sketch);
        }
        {
            var Q0;
            Q0 = qSketchRegion(id + "F30", true);
            extrude(context, id + "F31", {"entities" : qUnion([Q0]), "operationType" : NewBodyOperationType.REMOVE, "oppositeDirection" : true, "depth" : 4.15 * mm, "offsetDistance" : 25 * mm});
        }
        {
            var Q0;
            {var subQ0=sQuery(id+"F2.wireOp",EDGE,"E19.bottom");var subQ3=sQuery(id+"F2.wireOp",EDGE,"E14");var subQ5=sQuery(id+"F2.wireOp",EDGE,"E13");var subQ6=sQuery(id+"F2.wireOp",EDGE,"E12");var subQ20=sQuery(id+"F2.wireOp",EDGE,"E19.left");var subQ21=sQuery(id+"F2.wireOp",EDGE,"E18");var subQ24=sQuery(id+"F2.wireOp",EDGE,"E19.right");var subQ25=sQuery(id+"F2.wireOp",EDGE,"E19.top");var subQ26=sQuery(id+"F2.wireOp",EDGE,"E11");var subQ27=sQuery(id+"F2.wireOp",EDGE,"E20");var subQ28=sQuery(id+"F2.wireOp",EDGE,"E21");var subQ29=sQuery(id+"F2.wireOp",EDGE,"E17");var subQ30=sQuery(id+"F2.wireOp",EDGE,"E16");var subQ31=sQuery(id+"F2.wireOp",EDGE,"E15");var subQ32=makeQuery(id+"F3.opExtrude","CAP_FACE",FACE,{"disambiguationData":[OSD([subQ26,subQ6,subQ5,subQ3,subQ31,subQ30,subQ29,subQ21,subQ0,subQ25,subQ20,subQ24,subQ27,subQ28])],"isStart":true});Q0=makeQuery(id+"F23.boolean.opBoolean","MERGE",FACE,{"derivedFrom":[makeQuery(id+"F3.boolean.opBoolean","SPLIT",FACE,{"disambiguationData":[TD([makeQuery(id+"F3.opExtrude","SWEPT_FACE",FACE,{"disambiguationData":[OSD([subQ31])]})])],"derivedFrom":subQ32}),makeQuery(id+"F3.boolean.opBoolean","SPLIT",FACE,{"disambiguationData":[TD([makeQuery(id+"F3.opExtrude","SWEPT_FACE",FACE,{"disambiguationData":[OSD([subQ26])]})])],"derivedFrom":subQ32}),makeQuery(id+"F23.opExtrude","CAP_FACE",FACE,{"disambiguationData":[OSD([sQuery(id+"F22.wireOp",EDGE,"E47.bottom"),sQuery(id+"F22.wireOp",EDGE,"E47.top"),sQuery(id+"F22.wireOp",EDGE,"E47.left"),sQuery(id+"F22.wireOp",EDGE,"E47.right")])],"isStart":true})]});}
            var sketch = newSketch(context, id + "F32", { "sketchPlane" : qUnion([Q0])});
            skLineSegment(sketch, "E54.top", {"start": v(41, -17) * mm, "end": v(51, -17) * mm});
            skLineSegment(sketch, "E54.left", {"start": v(31, 9) * mm, "end": v(31, 2.5) * mm});
            skLineSegment(sketch, "E54.right", {"start": v(51, 9) * mm, "end": v(51, -17) * mm});
            skCircle(sketch, "E55", {"center": v(48.25, -14.25) * mm, "radius": 1.7 * mm});
            skCircle(sketch, "E56", {"center": v(48.25, 4.75) * mm, "radius": 1.7 * mm});
            skLineSegment(sketch, "E57", {"start": v(46.04, 2.5) * mm, "end": v(46.04, -10.31) * mm});
            skLineSegment(sketch, "E58", {"start": v(46.04, 2.5) * mm, "end": v(31, 2.5) * mm});
            skLineSegment(sketch, "E59", {"start": v(31, 2.5) * mm, "end": v(31, 9) * mm});
            skLineSegment(sketch, "E60", {"start": v(31, 9) * mm, "end": v(51, 9) * mm});
            skPoint(sketch, "E61.orphan", {"position": v(31, 23) * mm});
            skPoint(sketch, "E62.orphan", {"position": v(31, -17) * mm});
            skLineSegment(sketch, "E63", {"start": v(41, -17) * mm, "end": v(31, -17) * mm});
            skLineSegment(sketch, "E64", {"start": v(46.04, -10.31) * mm, "end": v(31, -10.31) * mm});
            skLineSegment(sketch, "E65", {"start": v(31, -10.31) * mm, "end": v(31, -17) * mm});
            skSolve(sketch);
        }
        {
            var Q0;
            Q0 = qSketchRegion(id + "F32", true);
            extrude(context, id + "F33", {"entities" : qUnion([Q0]), "operationType" : NewBodyOperationType.ADD, "depth" : 2 * mm, "offsetDistance" : 25 * mm});
        }
        {
            var Q0;
            Q0=makeQuery(id+"F33.opExtrude","CAP_FACE",FACE,{"disambiguationData":[OSD([sQuery(id+"F32.wireOp",EDGE,"E54.top"),sQuery(id+"F32.wireOp",EDGE,"E54.right"),sQuery(id+"F32.wireOp",EDGE,"E55"),sQuery(id+"F32.wireOp",EDGE,"E56"),sQuery(id+"F32.wireOp",EDGE,"E57"),sQuery(id+"F32.wireOp",EDGE,"crxLInDw-CmQ5-DDUw-NOyQ-Vxr8YGBbqhOr"),sQuery(id+"F32.wireOp",EDGE,"E58"),sQuery(id+"F32.wireOp",EDGE,"E59"),sQuery(id+"F32.wireOp",EDGE,"E60")])],"isStart":false});
            var sketch = newSketch(context, id + "F34", { "sketchPlane" : qUnion([Q0])});
            skCircle(sketch, "E66", {"center": v(48.25, 4.75) * mm, "radius": 1.7 * mm});
            skCircle(sketch, "E67", {"center": v(48.25, 4.75) * mm, "radius": 2.75 * mm});
            skCircle(sketch, "E68", {"center": v(48.25, -14.25) * mm, "radius": 2.75 * mm});
            skCircle(sketch, "E69", {"center": v(48.25, -14.25) * mm, "radius": 1.7 * mm});
            skSolve(sketch);
        }
        {
            var Q0;
            Q0 = qSketchRegion(id + "F34", true);
            extrude(context, id + "F35", {"entities" : qUnion([Q0]), "operationType" : NewBodyOperationType.ADD, "depth" : 2 * mm, "offsetDistance" : 25 * mm});
        }
        {
            var Q0;
            {var subQ0=sQuery(id+"F2.wireOp",EDGE,"E16");var subQ1=sQuery(id+"F2.wireOp",EDGE,"E14");var subQ2=sQuery(id+"F2.wireOp",EDGE,"E13");var subQ3=sQuery(id+"F2.wireOp",EDGE,"E12");var subQ4=sQuery(id+"F2.wireOp",EDGE,"E15");var subQ5=sQuery(id+"F0.wireOp",EDGE,"E0.bottom");var subQ6=sQuery(id+"F2.wireOp",EDGE,"E19.bottom");var subQ7=sQuery(id+"F2.wireOp",EDGE,"E17");var subQ9=sQuery(id+"F2.wireOp",EDGE,"E19.left");var subQ12=sQuery(id+"F2.wireOp",EDGE,"E19.right");var subQ13=sQuery(id+"F2.wireOp",EDGE,"E11");var subQ14=sQuery(id+"F2.wireOp",EDGE,"E18");var subQ15=sQuery(id+"F2.wireOp",EDGE,"E19.top");Q0=makeQuery(id+"F7.boolean.opBoolean","SPLIT",FACE,{"disambiguationData":[TD([makeQuery(id+"F1.opExtrude","SWEPT_FACE",FACE,{"disambiguationData":[OSD([subQ5])]})])],"derivedFrom":makeQuery(id+"F3.opExtrude","CAP_FACE",FACE,{"disambiguationData":[OSD([subQ13,subQ3,subQ2,subQ1,subQ4,subQ0,subQ7,subQ14,subQ6,subQ15,subQ9,subQ12,sQuery(id+"F2.wireOp",EDGE,"E20"),sQuery(id+"F2.wireOp",EDGE,"E21")])],"isStart":false})});}
            var sketch = newSketch(context, id + "F36", { "sketchPlane" : qUnion([Q0])});
            skLineSegment(sketch, "E70.bottom", {"start": v(-11, 15) * mm, "end": v(-8, 15) * mm});
            skLineSegment(sketch, "E70.top", {"start": v(-11, 3) * mm, "end": v(-8, 3) * mm});
            skLineSegment(sketch, "E70.left", {"start": v(-11, 15) * mm, "end": v(-11, 3) * mm});
            skLineSegment(sketch, "E70.right", {"start": v(-8, 15) * mm, "end": v(-8, 3) * mm});
            skSolve(sketch);
        }
        {
            var Q0;
            Q0 = qSketchRegion(id + "F36", true);
            extrude(context, id + "F37", {"entities" : qUnion([Q0]), "operationType" : NewBodyOperationType.ADD, "depth" : 10 * mm, "offsetDistance" : 25 * mm});
        }
        {
            var Q0;
            Q0=makeQuery(id+"F37.opExtrude","CAP_FACE",FACE,{"disambiguationData":[OSD([sQuery(id+"F36.wireOp",EDGE,"E70.bottom"),sQuery(id+"F36.wireOp",EDGE,"E70.top"),sQuery(id+"F36.wireOp",EDGE,"E70.left"),sQuery(id+"F36.wireOp",EDGE,"E70.right")])],"isStart":false});
            var sketch = newSketch(context, id + "F38", { "sketchPlane" : qUnion([Q0])});
            skLineSegment(sketch, "E71.bottom", {"start": v(-11, 15) * mm, "end": v(1, 15) * mm});
            skLineSegment(sketch, "E71.top", {"start": v(-11, 3) * mm, "end": v(1, 3) * mm});
            skLineSegment(sketch, "E71.left", {"start": v(-11, 15) * mm, "end": v(-11, 3) * mm});
            skLineSegment(sketch, "E71.right", {"start": v(1, 15) * mm, "end": v(1, 3) * mm});
            skSolve(sketch);
        }
        {
            var Q0;
            Q0 = qSketchRegion(id + "F38", true);
            extrude(context, id + "F39", {"entities" : qUnion([Q0]), "operationType" : NewBodyOperationType.ADD, "depth" : 4 * mm, "offsetDistance" : 25 * mm});
        }
    });
